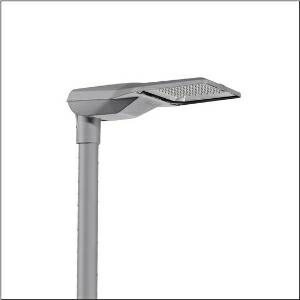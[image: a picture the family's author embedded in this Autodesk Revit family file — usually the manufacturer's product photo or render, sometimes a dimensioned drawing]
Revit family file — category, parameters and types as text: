
# Revit family: streetlight_sl_21_iq_midi___stw1_0a_5xe3e31d08nb_8d25
name_source: partatom
category: Lighting Fixtures
units: mm (PartAtom-declared; Revit-internal decimal feet)

## family parameters
Cut with Voids When Loaded = No
Host = Face
Light Source = No
Part Type = Normal
Room Calculation Point = No
Round Connector Dimension = Use Diameter
Shared = No

## types (1)
- --- (1 x LED, 23230 lm, 155.5 W, 3000K)
    Apparent Load = 155 VA
    CIE Flux Codes = 39 75 98 100 100
    Color Rendering = 70
    Color Temperature = 3000K
    Default Elevation = 1800 mm
    Description = Streetlight SL 21 iQ midi, mast luminaire, primary light control with lens, of PMMA, primary optical cover: cover, of toughened safety glass, transparent, light distribution: STW1.0a, light emission: direct distribution, primary light characteristic: asymmetric, installation type: post-top, side-entry, LED, High Power LED, rated luminous flux: 23.230lm, luminous efficacy: 149lm/W, light colour: 730, colour temperature: 3000K, control gear: iQ-Comfort, control: Auto-Match, Temp-Guard, Lumen-Switch, Night-Set, Smart-Wire, Light-Fading, Desk-Remote (wireless, voltage-free reading and setting of iQ features in the workshop via application-optimized NFC function/RFID function), optimised constant luminous flux control (CLO 2.0), pre-setting: linear dimming characteristic, mains connection: 230..240V, AC, 50/60Hz, start of lifetime: 156W, end of service life: 162W, reduction: 69W, luminaire housing, of diecast aluminium, powder-coated, SITECO metallic grey (DB 702S), corrosivity category C5 high according to DIN EN ISO 12944, please order mast flange separately, inclination adjustable: 0°, 5°, 10°, 15°, sealing non-destructively replaceable, multi-level sealing system, length: 644mm, width: 335mm, height: 110mm, mast flange for spigot size: 42mm (side-entry): 5XC10008XM4, 60/48mm (side-entry/post-top): 5XC10108XM2, 76/60mm (side-entry/post-top): 5XC10108XM1, mounting height: 4..8m, protection rating (complete): IP66, insulation class (complete): insulation class II (safety insulation), certification: CE, ENEC, ENEC+, VDE, impact resistance: IK10, permissible operating ambient temperature for outdoor applications: -40..+50°C, standard-compliant lighting for roads and squares, packaging unit: 1 piece

Light Distribution: STW1.0a
    Height = 111 mm
    Lamp = 1 x LED
    Lamp Light Flux = 23230 lm
    Lamp Power = 155.5 W
    Lamp count = 1
    Length = 644 mm
    Luminous efficacy = 149 lm/W
    Manufacturer = Siteco
    ModVariant = No
    Model = 5XE3E31D08NB
    Number of Poles = 1
    OnlyDefault = Yes
    Power Factor = 1
    Product Name = Streetlight SL 21 iQ midi | STW1.0a
    Product group = mast luminaire | pylon top
    ProductGroupID = 6100
    Protection Class = Protection class II
    Protection Degree = IP 66
    RLX_Detail_Level = 1
    RLX_Emergency_Light_Flux = 0 lm
    RLX_Emergency_Type = 0
    RLX_Emergency_Type_DB = No
    RlxData = <blob elided: 27293 chars, md5=c272c33e>
    Socket = socket
    Standby Power = 0 W
    System Light Flux = 23230 lm
    System Power = 155 W
    Type Comments = factory setting: luminous flux: 100 % | dim-lin: 254 | 823 mA
    Type Image = l_1004298.jpg
    URL = http://relux.com
    VarID = @adj_169401
    Voltage = 0 V
    Weight = 0.00 kg
    Width = 336 mm

## geometry (parser evidence)
native form markers: Blend x4, Sweep x13
no freeform markers — native parametric forms only
